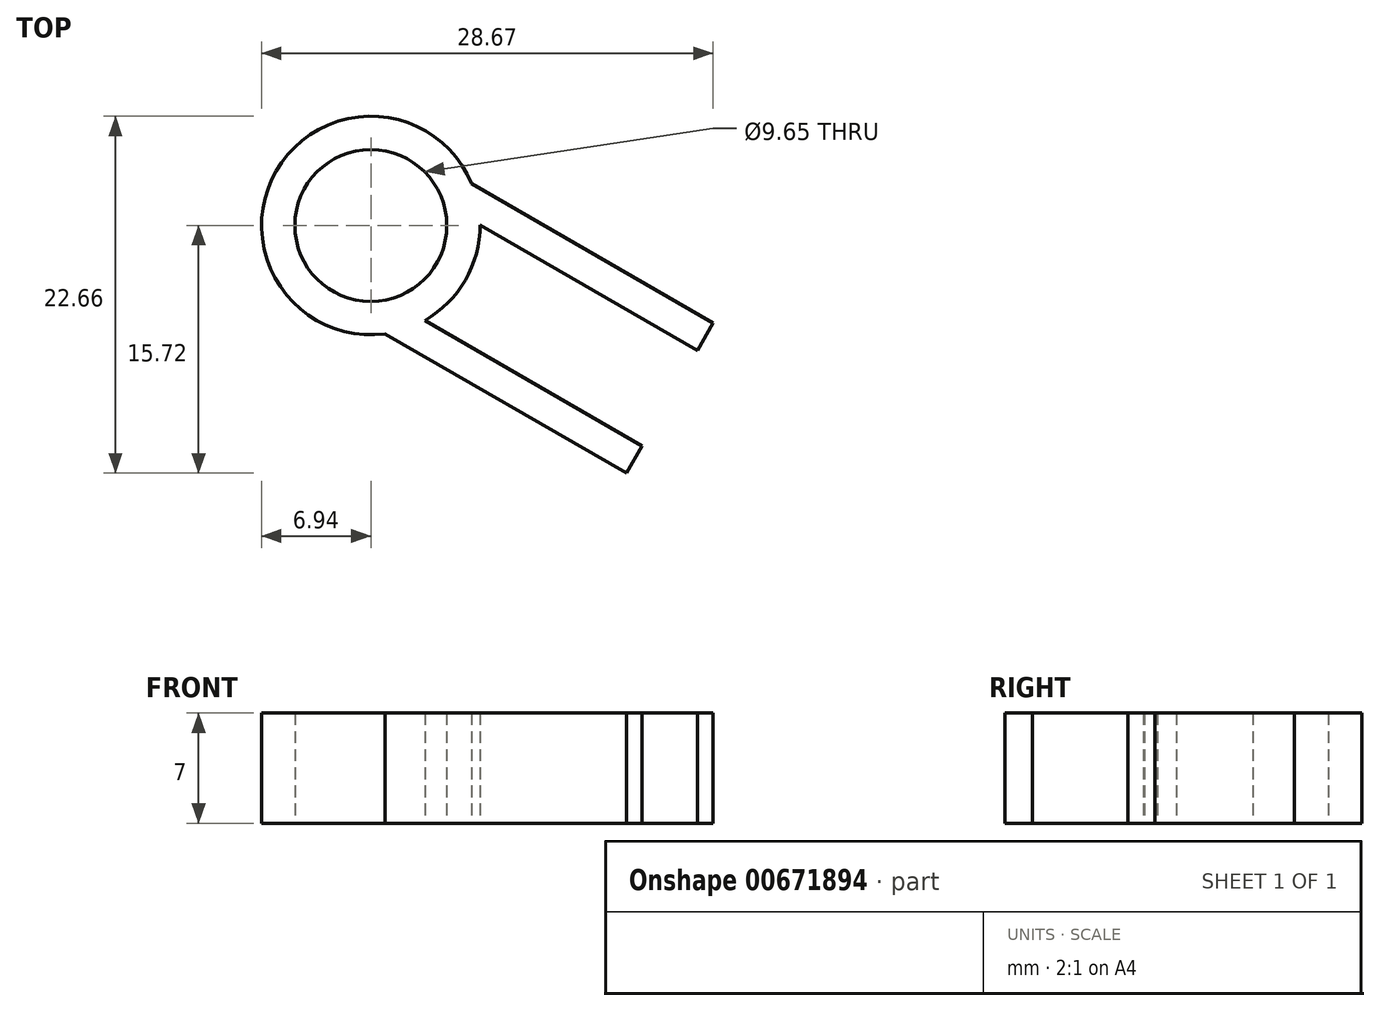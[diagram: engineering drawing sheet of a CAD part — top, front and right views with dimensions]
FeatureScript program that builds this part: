
annotation { "Feature Type Name" : "Feature", "Feature Type Description" : "" }
export const myFeature = defineFeature(function(context is Context, id is Id, definition is map)
    precondition{}
    {
        {
            var Q0;
            Q0=qCreatedBy(makeId("Top.planeOp"),FACE);
            var sketch = newSketch(context, id + "F0", { "sketchPlane" : qUnion([Q0])});
            skCircle(sketch, "E0", {"center": v(0, 0) * mm, "radius": 4.82 * mm});
            skCircle(sketch, "E1", {"center": v(0, 0) * mm, "radius": 6.94 * mm});
            skLineSegment(sketch, "E2", {"start": v(0, 0) * mm, "end": v(18.98, -10.96) * mm, "construction": true});
            skLineSegment(sketch, "E3", {"start": v(0, 0) * mm, "end": v(-14.74, -8.51) * mm, "construction": true});
            skLineSegment(sketch, "E4", {"start": v(0, 0) * mm, "end": v(0, 16.88) * mm, "construction": true});
            skLineSegment(sketch, "E5", {"start": v(18.98, -10.96) * mm, "end": v(21.73, -6.2) * mm, "construction": true});
            skLineSegment(sketch, "E6", {"start": v(18.98, -10.96) * mm, "end": v(16.23, -15.72) * mm, "construction": true});
            skLineSegment(sketch, "E7", {"start": v(16.23, -15.72) * mm, "end": v(0.91, -6.88) * mm});
            skLineSegment(sketch, "E8", {"start": v(21.73, -6.2) * mm, "end": v(6.41, 2.65) * mm});
            skLineSegment(sketch, "E9", {"start": v(20.73, -7.93) * mm, "end": v(6.94, 0.04) * mm});
            skLineSegment(sketch, "E10", {"start": v(17.23, -14) * mm, "end": v(3.44, -6.03) * mm});
            skLineSegment(sketch, "E11", {"start": v(20.73, -7.93) * mm, "end": v(21.73, -6.2) * mm});
            skLineSegment(sketch, "E12", {"start": v(16.23, -15.72) * mm, "end": v(17.23, -14) * mm});
            skSolve(sketch);
        }
        {
            var Q0;
            Q0=makeQuery(id+"F0.imprint","IMPRINT",FACE,{"disambiguationData":[TD([[makeQuery(id+"F0.imprint","IMPRINT",EDGE,{"derivedFrom":sQuery(id+"F0.wireOp",EDGE,"E0")}),-1.0]])]});
            var Q1;
            {var subQ0=sQuery(id+"F0.wireOp",EDGE,"E7");Q1=makeQuery(id+"F0.imprint","IMPRINT",FACE,{"disambiguationData":[TD([[makeQuery(id+"F0.imprint","IMPRINT",EDGE,{"derivedFrom":subQ0}),-1.0]])]});}
            var Q2;
            {var subQ0=sQuery(id+"F0.wireOp",EDGE,"E8");Q2=makeQuery(id+"F0.imprint","IMPRINT",FACE,{"disambiguationData":[TD([[makeQuery(id+"F0.imprint","IMPRINT",EDGE,{"derivedFrom":subQ0}),1.0]])]});}
            extrude(context, id + "F1", {"entities" : qUnion([Q0, Q1, Q2]), "depth" : 7 * mm, "offsetDistance" : 25 * mm});
        }
    });
